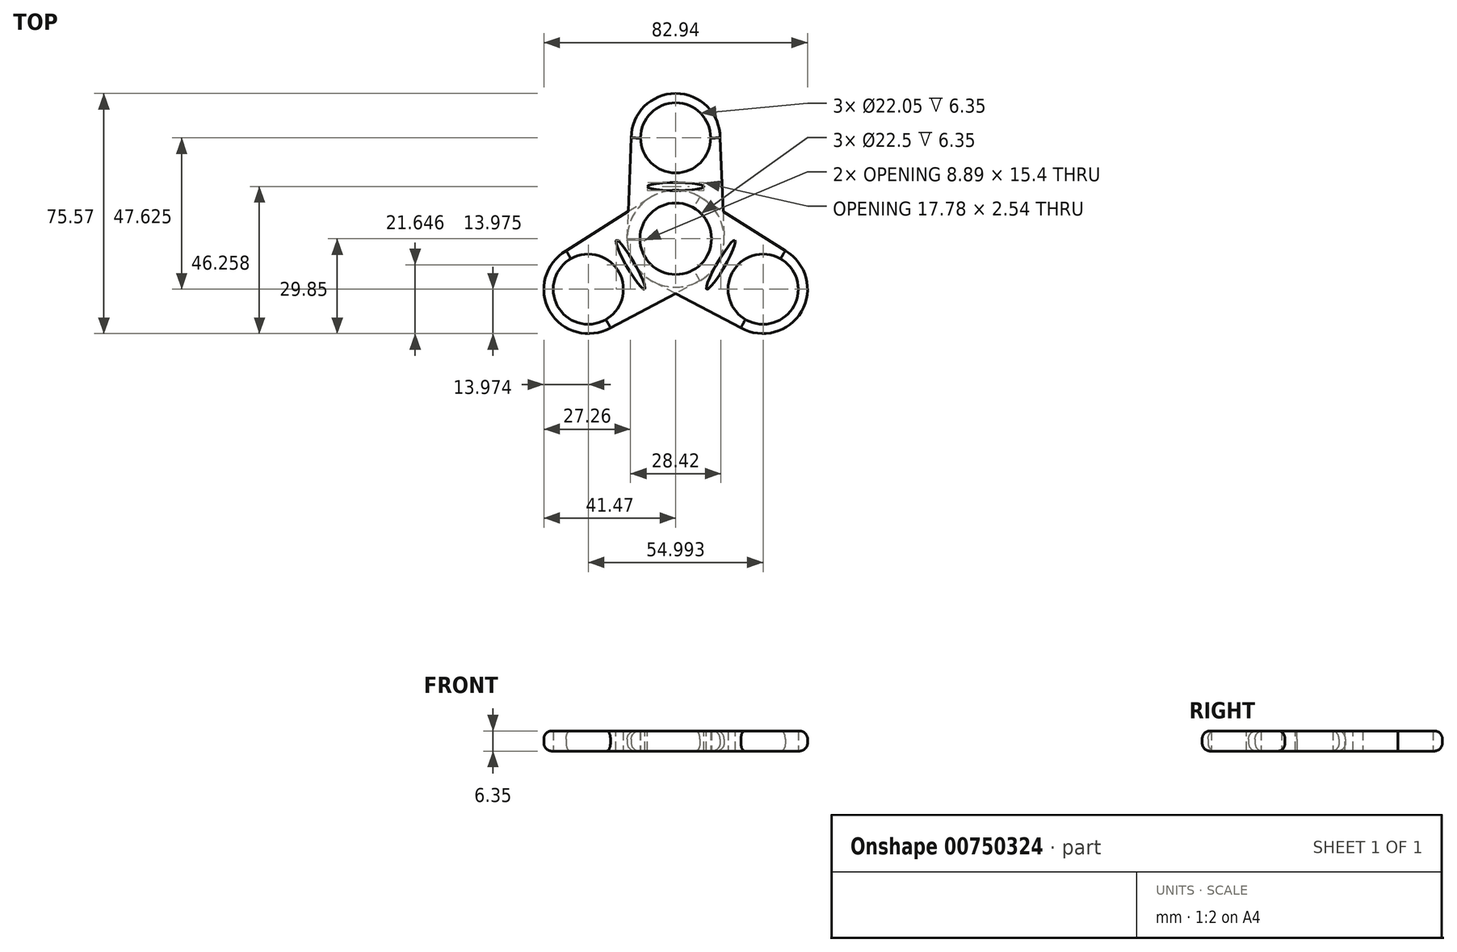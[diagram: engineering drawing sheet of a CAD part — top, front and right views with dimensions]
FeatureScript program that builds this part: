
annotation { "Feature Type Name" : "Feature", "Feature Type Description" : "" }
export const myFeature = defineFeature(function(context is Context, id is Id, definition is map)
    precondition{}
    {
        {
            var Q0;
            Q0=qCreatedBy(makeId("Top.planeOp"),FACE);
            var sketch = newSketch(context, id + "F0", { "sketchPlane" : qUnion([Q0])});
            skCircle(sketch, "E0", {"center": v(0, 0) * mm, "radius": 15.24 * mm});
            skCircle(sketch, "E1", {"center": v(0, 0) * mm, "radius": 11.25 * mm});
            skCircle(sketch, "E2", {"center": v(0, 31.75) * mm, "radius": 13.97 * mm});
            skCircle(sketch, "E3", {"center": v(0, 31.75) * mm, "radius": 11.02 * mm});
            skLineSegment(sketch, "E4", {"start": v(-13.97, 31.75) * mm, "end": v(13.97, 31.75) * mm});
            skLineSegment(sketch, "E5", {"start": v(13.97, 31.75) * mm, "end": v(15.25, 0) * mm});
            skLineSegment(sketch, "E6", {"start": v(15.25, 0) * mm, "end": v(-15.24, 0) * mm});
            skLineSegment(sketch, "E7", {"start": v(-15.24, 0) * mm, "end": v(-13.97, 31.75) * mm});
            skSolve(sketch);
        }
        {
            var Q0;
            {var subQ0=sQuery(id+"F0.wireOp",EDGE,"E4");var subQ4=sQuery(id+"F0.wireOp",EDGE,"E3");var subQ5=makeQuery(id+"F0.imprint","INTERSECT",VERTEX,{"disambiguationData":[OD(0.0)],"derivedFrom":[subQ4,subQ0]});Q0=makeQuery(id+"F0.imprint","IMPRINT",FACE,{"disambiguationData":[TD([[makeQuery(id+"F0.imprint","IMPRINT",EDGE,{"disambiguationData":[TD([[subQ5,1.0]])],"derivedFrom":subQ4}),-1.0]])]});}
            var Q1;
            {var subQ0=sQuery(id+"F0.wireOp",EDGE,"E5");var subQ1=sQuery(id+"F0.wireOp",EDGE,"E0");var subQ2=makeQuery(id+"F0.imprint","INTERSECT",VERTEX,{"derivedFrom":[subQ1,subQ0]});Q1=makeQuery(id+"F0.imprint","IMPRINT",FACE,{"disambiguationData":[TD([[makeQuery(id+"F0.imprint","IMPRINT",EDGE,{"disambiguationData":[TD([[subQ2,-1.0]])],"derivedFrom":subQ1}),-1.0]])]});}
            var Q2;
            {var subQ0=sQuery(id+"F0.wireOp",EDGE,"E4");var subQ4=sQuery(id+"F0.wireOp",EDGE,"E3");var subQ6=makeQuery(id+"F0.imprint","INTERSECT",VERTEX,{"disambiguationData":[OD(0.0)],"derivedFrom":[subQ4,subQ0]});Q2=makeQuery(id+"F0.imprint","IMPRINT",FACE,{"disambiguationData":[TD([[makeQuery(id+"F0.imprint","IMPRINT",EDGE,{"disambiguationData":[TD([[subQ6,-1.0]])],"derivedFrom":subQ4}),-1.0]])]});}
            var Q3;
            {var subQ4=sQuery(id+"F0.wireOp",EDGE,"E0");var subQ6=makeQuery(id+"F0.imprint","INTERSECT",VERTEX,{"derivedFrom":[subQ4,sQuery(id+"F0.wireOp",EDGE,"E5")]});Q3=makeQuery(id+"F0.imprint","IMPRINT",FACE,{"disambiguationData":[TD([[makeQuery(id+"F0.imprint","IMPRINT",EDGE,{"disambiguationData":[TD([[subQ6,1.0]])],"derivedFrom":subQ4}),1.0]])]});}
            var Q4;
            {var subQ0=sQuery(id+"F0.wireOp",EDGE,"E6");var subQ4=sQuery(id+"F0.wireOp",EDGE,"E1");var subQ6=makeQuery(id+"F0.imprint","INTERSECT",VERTEX,{"disambiguationData":[OD(0.0)],"derivedFrom":[subQ4,subQ0]});Q4=makeQuery(id+"F0.imprint","IMPRINT",FACE,{"disambiguationData":[TD([[makeQuery(id+"F0.imprint","IMPRINT",EDGE,{"disambiguationData":[TD([[subQ6,1.0]])],"derivedFrom":subQ4}),-1.0]])]});}
            extrude(context, id + "F1", {"entities" : qUnion([Q0, Q1, Q2, Q3, Q4]), "depth" : 6.35 * mm, "offsetDistance" : 25.4 * mm});
        }
        {
            var Q0;
            Q0=makeQuery(id+"F1.opExtrude","CAP_FACE",FACE,{"disambiguationData":[OSD([sQuery(id+"F0.wireOp",EDGE,"E0"),sQuery(id+"F0.wireOp",EDGE,"E1"),sQuery(id+"F0.wireOp",EDGE,"E2"),sQuery(id+"F0.wireOp",EDGE,"E3"),sQuery(id+"F0.wireOp",EDGE,"E5"),sQuery(id+"F0.wireOp",EDGE,"E7")])],"isStart":false});
            var sketch = newSketch(context, id + "F2", { "sketchPlane" : qUnion([Q0])});
            skEllipse(sketch, "E8", {"center": v(0, 16.4) * mm, "majorRadius": 8.9 * mm, "minorRadius": 1.27 * mm, "majorAxis": v(-1, 0)});
            skSolve(sketch);
        }
        {
            var Q0;
            Q0=makeQuery(id+"F2.imprint","IMPRINT",FACE,{"disambiguationData":[TD([[makeQuery(id+"F2.imprint","IMPRINT",EDGE,{"derivedFrom":sQuery(id+"F2.wireOp",EDGE,"E8")}),1.0]])]});
            extrude(context, id + "F3", {"entities" : qUnion([Q0]), "operationType" : NewBodyOperationType.REMOVE, "oppositeDirection" : true, "depth" : 6.35 * mm, "offsetDistance" : 25.4 * mm});
        }
        {
            var Q0;
            Q0=makeQuery(id+"F1.opExtrude","SWEPT_BODY",BODY,{"disambiguationData":[OSD([sQuery(id+"F0.wireOp",EDGE,"E0"),sQuery(id+"F0.wireOp",EDGE,"E1"),sQuery(id+"F0.wireOp",EDGE,"E2"),sQuery(id+"F0.wireOp",EDGE,"E3"),sQuery(id+"F0.wireOp",EDGE,"E5"),sQuery(id+"F0.wireOp",EDGE,"E7")])]});
            var Q1;
            Q1=makeQuery(id+"F1.opExtrude","CAP_EDGE",EDGE,{"disambiguationData":[OSD([sQuery(id+"F0.wireOp",EDGE,"E1")])],"isStart":false});
            circularPattern(context, id + "F4", {"entities" : qUnion([Q0]), "axis" : qUnion([Q1]), "angle" : 360 * degree, "instanceCount" : 3, "equalSpace" : true});
        }
        {
            var Q0;
            Q0=makeQuery(id+"F4.opPattern","COPY",EDGE,{"derivedFrom":makeQuery(id+"F1.opExtrude","CAP_EDGE",EDGE,{"disambiguationData":[OSD([sQuery(id+"F0.wireOp",EDGE,"E2")])],"isStart":false}),"instanceName":"1"});
            var Q1;
            Q1=makeQuery(id+"F4.opPattern","COPY",EDGE,{"derivedFrom":makeQuery(id+"F1.opExtrude","CAP_EDGE",EDGE,{"disambiguationData":[OSD([sQuery(id+"F0.wireOp",EDGE,"E7")])],"isStart":false}),"instanceName":"1"});
            var Q2;
            Q2=makeQuery(id+"F4.opPattern","COPY",EDGE,{"derivedFrom":makeQuery(id+"F1.opExtrude","CAP_EDGE",EDGE,{"disambiguationData":[OSD([sQuery(id+"F0.wireOp",EDGE,"E5")])],"isStart":false}),"instanceName":"1"});
            var Q3;
            Q3=makeQuery(id+"F1.opExtrude","CAP_EDGE",EDGE,{"disambiguationData":[OSD([sQuery(id+"F0.wireOp",EDGE,"E7")])],"isStart":false});
            var Q4;
            Q4=makeQuery(id+"F1.opExtrude","CAP_EDGE",EDGE,{"disambiguationData":[OSD([sQuery(id+"F0.wireOp",EDGE,"E2")])],"isStart":false});
            var Q5;
            Q5=makeQuery(id+"F1.opExtrude","CAP_EDGE",EDGE,{"disambiguationData":[OSD([sQuery(id+"F0.wireOp",EDGE,"E5")])],"isStart":false});
            var Q6;
            Q6=makeQuery(id+"F4.opPattern","COPY",EDGE,{"derivedFrom":makeQuery(id+"F1.opExtrude","CAP_EDGE",EDGE,{"disambiguationData":[OSD([sQuery(id+"F0.wireOp",EDGE,"E7")])],"isStart":false}),"instanceName":"2"});
            var Q7;
            Q7=makeQuery(id+"F4.opPattern","COPY",EDGE,{"derivedFrom":makeQuery(id+"F1.opExtrude","CAP_EDGE",EDGE,{"disambiguationData":[OSD([sQuery(id+"F0.wireOp",EDGE,"E2")])],"isStart":false}),"instanceName":"2"});
            var Q8;
            Q8=makeQuery(id+"F4.opPattern","COPY",EDGE,{"derivedFrom":makeQuery(id+"F1.opExtrude","CAP_EDGE",EDGE,{"disambiguationData":[OSD([sQuery(id+"F0.wireOp",EDGE,"E5")])],"isStart":false}),"instanceName":"2"});
            var Q9;
            Q9=makeQuery(id+"F1.opExtrude","CAP_EDGE",EDGE,{"disambiguationData":[OSD([sQuery(id+"F0.wireOp",EDGE,"E5")])],"isStart":true});
            var Q10;
            Q10=makeQuery(id+"F1.opExtrude","CAP_EDGE",EDGE,{"disambiguationData":[OSD([sQuery(id+"F0.wireOp",EDGE,"E2")])],"isStart":true});
            var Q11;
            Q11=makeQuery(id+"F1.opExtrude","CAP_EDGE",EDGE,{"disambiguationData":[OSD([sQuery(id+"F0.wireOp",EDGE,"E7")])],"isStart":true});
            var Q12;
            Q12=makeQuery(id+"F4.opPattern","COPY",EDGE,{"derivedFrom":makeQuery(id+"F1.opExtrude","CAP_EDGE",EDGE,{"disambiguationData":[OSD([sQuery(id+"F0.wireOp",EDGE,"E5")])],"isStart":true}),"instanceName":"1"});
            var Q13;
            Q13=makeQuery(id+"F4.opPattern","COPY",EDGE,{"derivedFrom":makeQuery(id+"F1.opExtrude","CAP_EDGE",EDGE,{"disambiguationData":[OSD([sQuery(id+"F0.wireOp",EDGE,"E2")])],"isStart":true}),"instanceName":"1"});
            var Q14;
            Q14=makeQuery(id+"F4.opPattern","COPY",EDGE,{"derivedFrom":makeQuery(id+"F1.opExtrude","CAP_EDGE",EDGE,{"disambiguationData":[OSD([sQuery(id+"F0.wireOp",EDGE,"E7")])],"isStart":true}),"instanceName":"1"});
            var Q15;
            Q15=makeQuery(id+"F4.opPattern","COPY",EDGE,{"derivedFrom":makeQuery(id+"F1.opExtrude","CAP_EDGE",EDGE,{"disambiguationData":[OSD([sQuery(id+"F0.wireOp",EDGE,"E5")])],"isStart":true}),"instanceName":"2"});
            var Q16;
            Q16=makeQuery(id+"F4.opPattern","COPY",EDGE,{"derivedFrom":makeQuery(id+"F1.opExtrude","CAP_EDGE",EDGE,{"disambiguationData":[OSD([sQuery(id+"F0.wireOp",EDGE,"E2")])],"isStart":true}),"instanceName":"2"});
            var Q17;
            Q17=makeQuery(id+"F4.opPattern","COPY",EDGE,{"derivedFrom":makeQuery(id+"F1.opExtrude","CAP_EDGE",EDGE,{"disambiguationData":[OSD([sQuery(id+"F0.wireOp",EDGE,"E7")])],"isStart":true}),"instanceName":"2"});
            fillet(context, id + "F5", {"entities" : qUnion([Q0, Q1, Q2, Q3, Q4, Q5, Q6, Q7, Q8, Q9, Q10, Q11, Q12, Q13, Q14, Q15, Q16, Q17]), "radius" : 2.54 * mm, "tangentPropagation" : true, "allowEdgeOverflow" : false});
        }
    });
